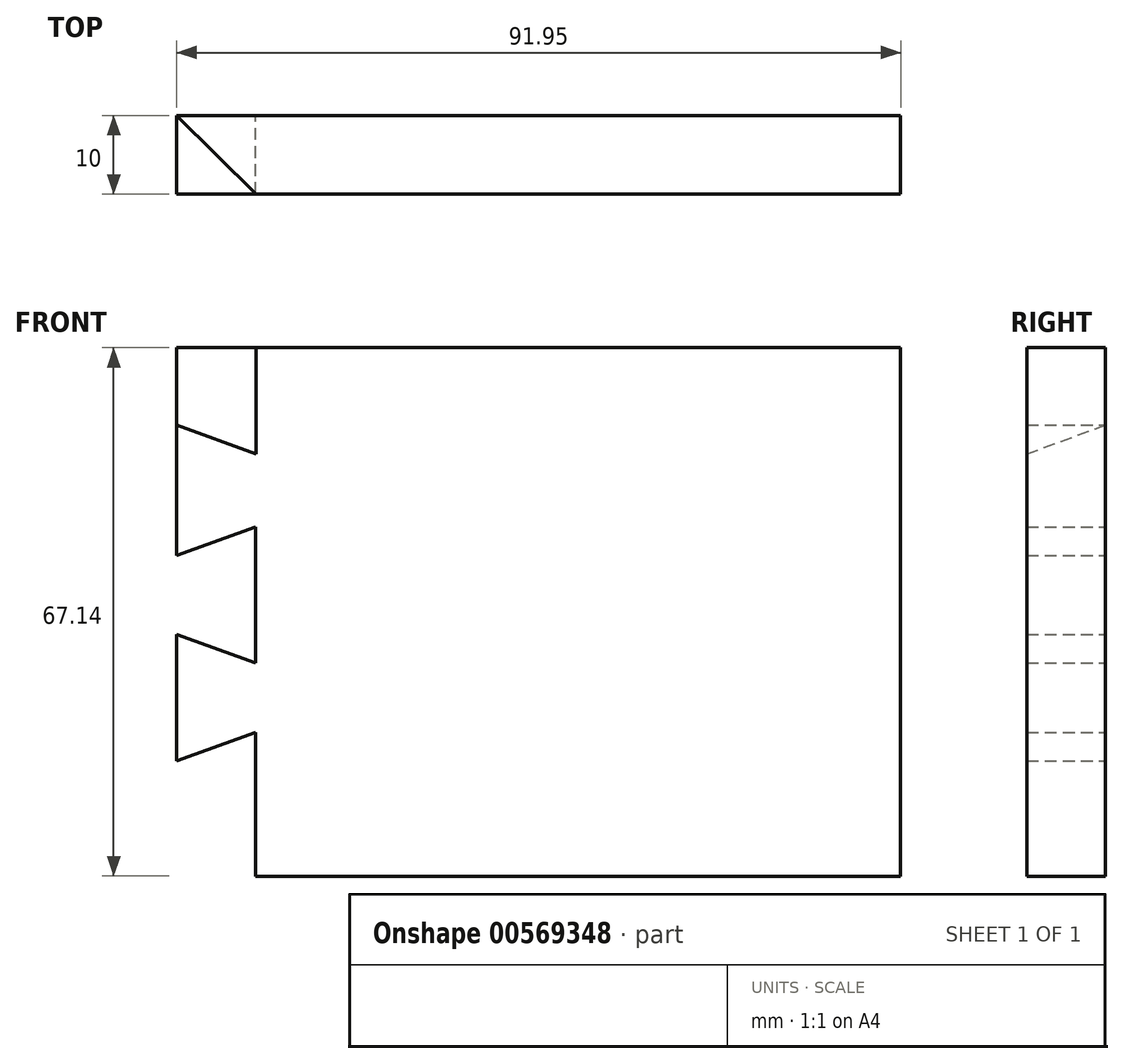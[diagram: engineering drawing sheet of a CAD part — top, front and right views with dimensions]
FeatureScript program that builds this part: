
annotation { "Feature Type Name" : "Feature", "Feature Type Description" : "" }
export const myFeature = defineFeature(function(context is Context, id is Id, definition is map)
    precondition{}
    {
        {
            var Q0;
            Q0=qCreatedBy(makeId("Front.planeOp"),FACE);
            var sketch = newSketch(context, id + "F0", { "sketchPlane" : qUnion([Q0])});
            skLineSegment(sketch, "E0", {"start": v(-52.23, 36.87) * mm, "end": v(29.64, 36.87) * mm});
            skLineSegment(sketch, "E1", {"start": v(29.64, 36.87) * mm, "end": v(29.64, -30.27) * mm});
            skLineSegment(sketch, "E2", {"start": v(29.64, -30.27) * mm, "end": v(-52.31, -30.27) * mm});
            skLineSegment(sketch, "E3", {"start": v(-52.31, -30.27) * mm, "end": v(-52.31, -12) * mm});
            skLineSegment(sketch, "E4", {"start": v(-52.31, -12) * mm, "end": v(-62.31, -15.64) * mm});
            skLineSegment(sketch, "E5", {"start": v(-62.31, -15.64) * mm, "end": v(-62.31, 0.46) * mm});
            skLineSegment(sketch, "E6", {"start": v(-62.31, 0.46) * mm, "end": v(-52.31, -3.18) * mm});
            skLineSegment(sketch, "E7", {"start": v(-52.31, -3.18) * mm, "end": v(-52.31, 14.1) * mm});
            skLineSegment(sketch, "E8", {"start": v(-52.31, 14.1) * mm, "end": v(-62.31, 10.46) * mm});
            skLineSegment(sketch, "E9", {"start": v(-62.31, 10.46) * mm, "end": v(-62.31, 27.04) * mm});
            skLineSegment(sketch, "E10", {"start": v(-62.31, 27.04) * mm, "end": v(-52.23, 23.37) * mm});
            skLineSegment(sketch, "E11", {"start": v(-52.23, 23.37) * mm, "end": v(-52.23, 36.87) * mm});
            skSolve(sketch);
        }
        {
            var Q0;
            Q0=makeQuery(id+"F0.imprint","IMPRINT",FACE,{"disambiguationData":[TD([[makeQuery(id+"F0.imprint","IMPRINT",EDGE,{"derivedFrom":sQuery(id+"F0.wireOp",EDGE,"E0")}),-1.0]])]});
            extrude(context, id + "F1", {"entities" : qUnion([Q0]), "depth" : 10 * mm, "offsetDistance" : 25 * mm});
        }
        {
            var Q0;
            Q0=makeQuery(id+"F1.opExtrude","SWEPT_FACE",FACE,{"disambiguationData":[OSD([sQuery(id+"F0.wireOp",EDGE,"E0")])]});
            var sketch = newSketch(context, id + "F2", { "sketchPlane" : qUnion([Q0])});
            skLineSegment(sketch, "E12", {"start": v(-52.23, 0) * mm, "end": v(-62.31, 0) * mm});
            skLineSegment(sketch, "E13", {"start": v(-62.31, 0) * mm, "end": v(-52.23, -10) * mm});
            skLineSegment(sketch, "E14", {"start": v(-52.23, -10) * mm, "end": v(-52.23, 0) * mm});
            skSolve(sketch);
        }
        {
            var Q0;
            Q0=makeQuery(id+"F2.imprint","IMPRINT",FACE,{"disambiguationData":[TD([[makeQuery(id+"F2.imprint","IMPRINT",EDGE,{"derivedFrom":sQuery(id+"F2.wireOp",EDGE,"E14")}),-1.0]])]});
            var sketch = newSketch(context, id + "F3", { "sketchPlane" : qUnion([Q0])});
            skSolve(sketch);
        }
        {
            var Q0;
            Q0 = qSketchRegion(id + "F3", true);
            var Q1;
            Q1=makeQuery(id+"F2.imprint","IMPRINT",FACE,{"disambiguationData":[TD([[makeQuery(id+"F2.imprint","IMPRINT",EDGE,{"derivedFrom":sQuery(id+"F2.wireOp",EDGE,"E12")}),1.0]])]});
            extrude(context, id + "F4", {"entities" : qUnion([Q0, Q1]), "operationType" : NewBodyOperationType.ADD, "endBound" : BoundingType.UP_TO_NEXT, "oppositeDirection" : true, "depth" : 25 * mm, "offsetDistance" : 25 * mm});
        }
    });
